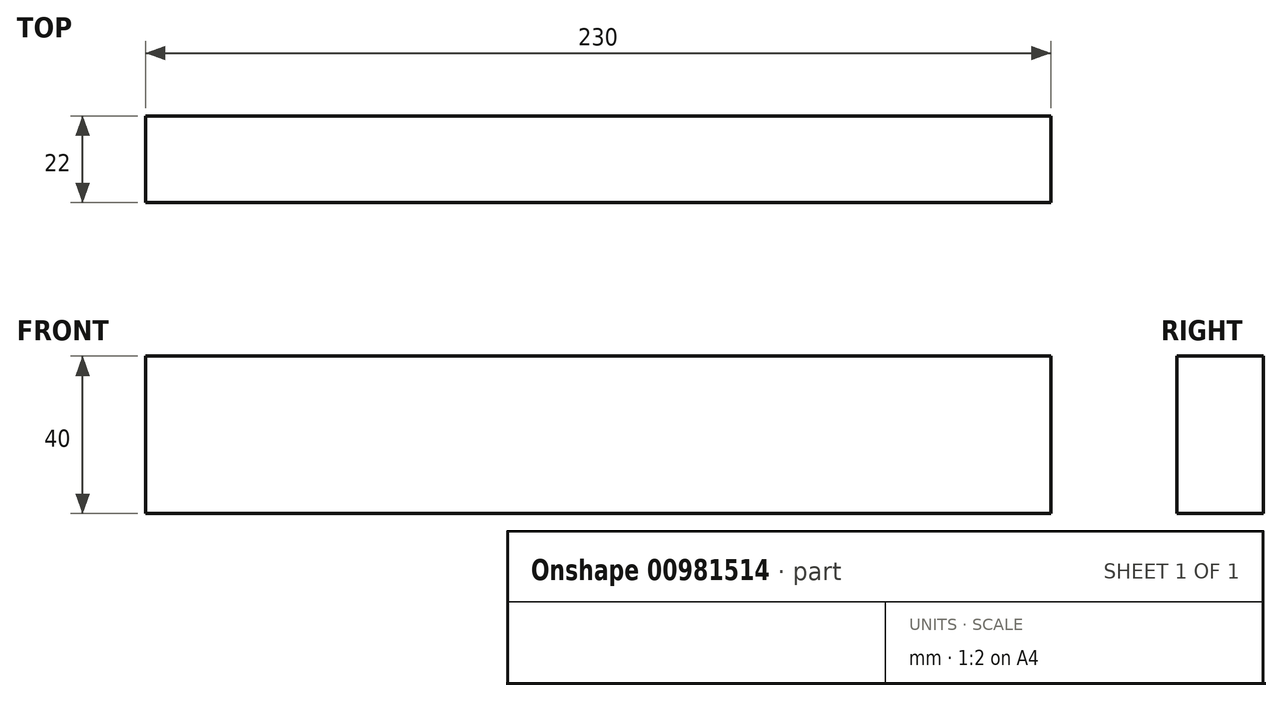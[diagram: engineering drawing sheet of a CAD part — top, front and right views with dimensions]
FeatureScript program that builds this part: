
annotation { "Feature Type Name" : "Feature", "Feature Type Description" : "" }
export const myFeature = defineFeature(function(context is Context, id is Id, definition is map)
    precondition{}
    {
        {
            var Q0;
            Q0=qCreatedBy(makeId("Right.planeOp"),FACE);
            var sketch = newSketch(context, id + "F0", { "sketchPlane" : qUnion([Q0])});
            skLineSegment(sketch, "E0.bottom", {"start": v(-30.65, 67.88) * mm, "end": v(-8.65, 67.88) * mm});
            skLineSegment(sketch, "E0.top", {"start": v(-30.65, 27.88) * mm, "end": v(-8.65, 27.88) * mm});
            skLineSegment(sketch, "E0.left", {"start": v(-30.65, 67.88) * mm, "end": v(-30.65, 27.88) * mm});
            skLineSegment(sketch, "E0.right", {"start": v(-8.65, 67.88) * mm, "end": v(-8.65, 27.88) * mm});
            skLineSegment(sketch, "E1.bottom", {"start": v(-30.65, 63.88) * mm, "end": v(-20.65, 63.88) * mm});
            skLineSegment(sketch, "E1.top", {"start": v(-30.65, 55.88) * mm, "end": v(-20.65, 55.88) * mm});
            skLineSegment(sketch, "E1.left", {"start": v(-30.65, 63.88) * mm, "end": v(-30.65, 55.88) * mm});
            skLineSegment(sketch, "E1.right", {"start": v(-20.65, 63.88) * mm, "end": v(-20.65, 55.88) * mm});
            skSolve(sketch);
        }
        {
            var Q0;
            Q0=makeQuery(id+"F0.imprint","IMPRINT",FACE,{"disambiguationData":[TD([[makeQuery(id+"F0.imprint","IMPRINT",EDGE,{"derivedFrom":sQuery(id+"F0.wireOp",EDGE,"E1.bottom")}),-1.0]])]});
            var Q1;
            {var subQ4=sQuery(id+"F0.wireOp",EDGE,"E0.bottom");Q1=makeQuery(id+"F0.imprint","IMPRINT",FACE,{"disambiguationData":[TD([[makeQuery(id+"F0.imprint","IMPRINT",EDGE,{"derivedFrom":subQ4}),-1.0]])]});}
            extrude(context, id + "F1", {"entities" : qUnion([Q0, Q1]), "depth" : 230 * mm, "offsetDistance" : 25 * mm});
        }
    });
